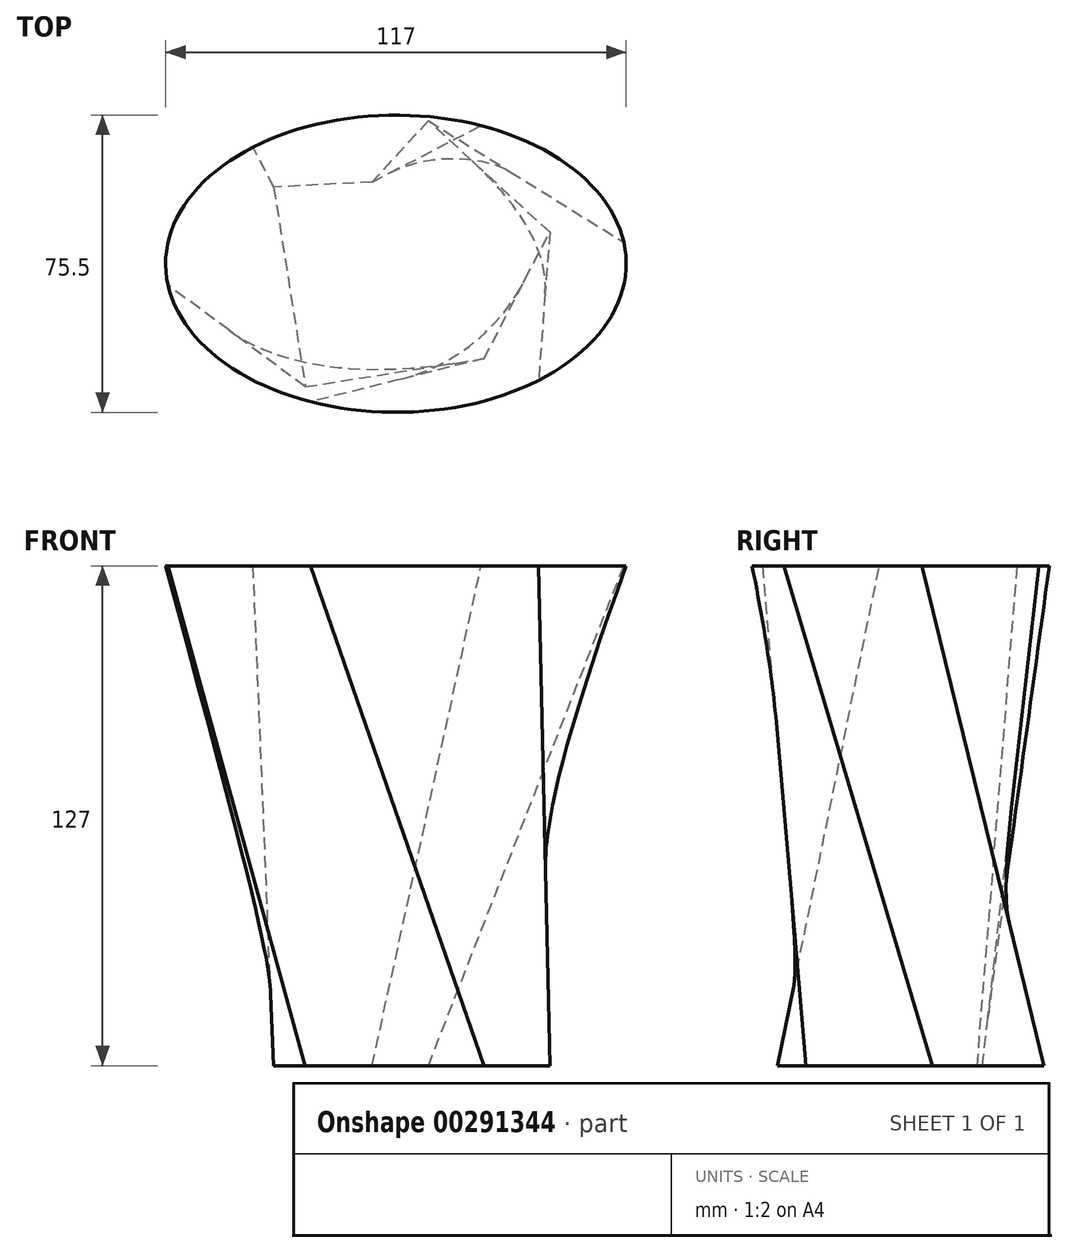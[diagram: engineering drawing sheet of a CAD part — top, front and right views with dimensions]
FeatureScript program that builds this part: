
annotation { "Feature Type Name" : "Feature", "Feature Type Description" : "" }
export const myFeature = defineFeature(function(context is Context, id is Id, definition is map)
    precondition{}
    {
        {
            var Q0;
            Q0=qCreatedBy(makeId("Top.planeOp"),FACE);
            cPlane(context, id + "F0", {"entities" : qUnion([Q0]), "cplaneType" : CPlaneType.OFFSET, "offset" : 127 * mm, "width" : 152.4 * mm, "height" : 152.4 * mm});
        }
        {
            var Q0;
            Q0=qCreatedBy(makeId("Top.planeOp"),FACE);
            var sketch = newSketch(context, id + "F1", { "sketchPlane" : qUnion([Q0])});
            skLineSegment(sketch, "E0", {"start": v(-31.06, 19.44) * mm, "end": v(-23.03, -31.27) * mm});
            skLineSegment(sketch, "E1", {"start": v(-23.03, -31.27) * mm, "end": v(22.38, -24.08) * mm});
            skLineSegment(sketch, "E2", {"start": v(22.38, -24.08) * mm, "end": v(39.08, 8.03) * mm});
            skLineSegment(sketch, "E3", {"start": v(39.08, 8.03) * mm, "end": v(8.24, 36.34) * mm});
            skLineSegment(sketch, "E4", {"start": v(8.24, 36.34) * mm, "end": v(-6.03, 20.8) * mm});
            skLineSegment(sketch, "E5", {"start": v(-6.03, 20.8) * mm, "end": v(-31.06, 19.44) * mm});
            skSolve(sketch);
        }
        {
            var Q0;
            Q0=qCreatedBy(id+"F0.planeOp",FACE);
            var sketch = newSketch(context, id + "F2", { "sketchPlane" : qUnion([Q0])});
            skEllipse(sketch, "E6", {"center": v(0, 0) * mm, "majorRadius": 58.5 * mm, "minorRadius": 37.75 * mm, "majorAxis": v(1, 0)});
            skSolve(sketch);
        }
        {
            var Q0;
            Q0 = qSketchRegion(id + "F1", true);
            var Q1;
            Q1 = qSketchRegion(id + "F2", true);
            loft(context, id + "F3", {"sheetProfilesArray" : [{ "sheetProfileEntities" : qUnion([Q0]) }, { "sheetProfileEntities" : qUnion([Q1]) }]});
        }
    });
